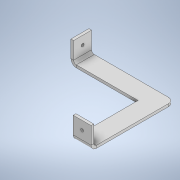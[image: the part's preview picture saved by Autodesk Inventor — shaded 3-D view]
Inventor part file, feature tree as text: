
AUTODESK INVENTOR PART (.ipt)
format: ipt  version: 2021 (Build 250183000, 183)  size: 151,552 bytes
history: native  units: mm
features: other x7, sketch x4, hole x2
ambient origin geometry x8: Origin, YZ Plane, XZ Plane, XY Plane, X Axis, Y Axis, Z Axis, Center Point
bodies: Body1 (feature_tree)
feature tree (13):
  other  "實體1"
  other  "轉角外圓角1"
  other  "凸緣1"
  hole  "孔1"  [1 undecoded]
  hole  "孔2"  [1 undecoded]
  sketch  "草圖1"
  other  "平板1"
  sketch  "草圖2"
  other  "平板2"
  other  "折彎1"
  other  "轉角1"
  sketch  "草圖3"
  sketch  "草圖4"
note: 2 required parameter values undecoded (feature->parameter linkage not recoverable at this tier; creation-order binding heuristic only, values carry confidence <= 0.55)
